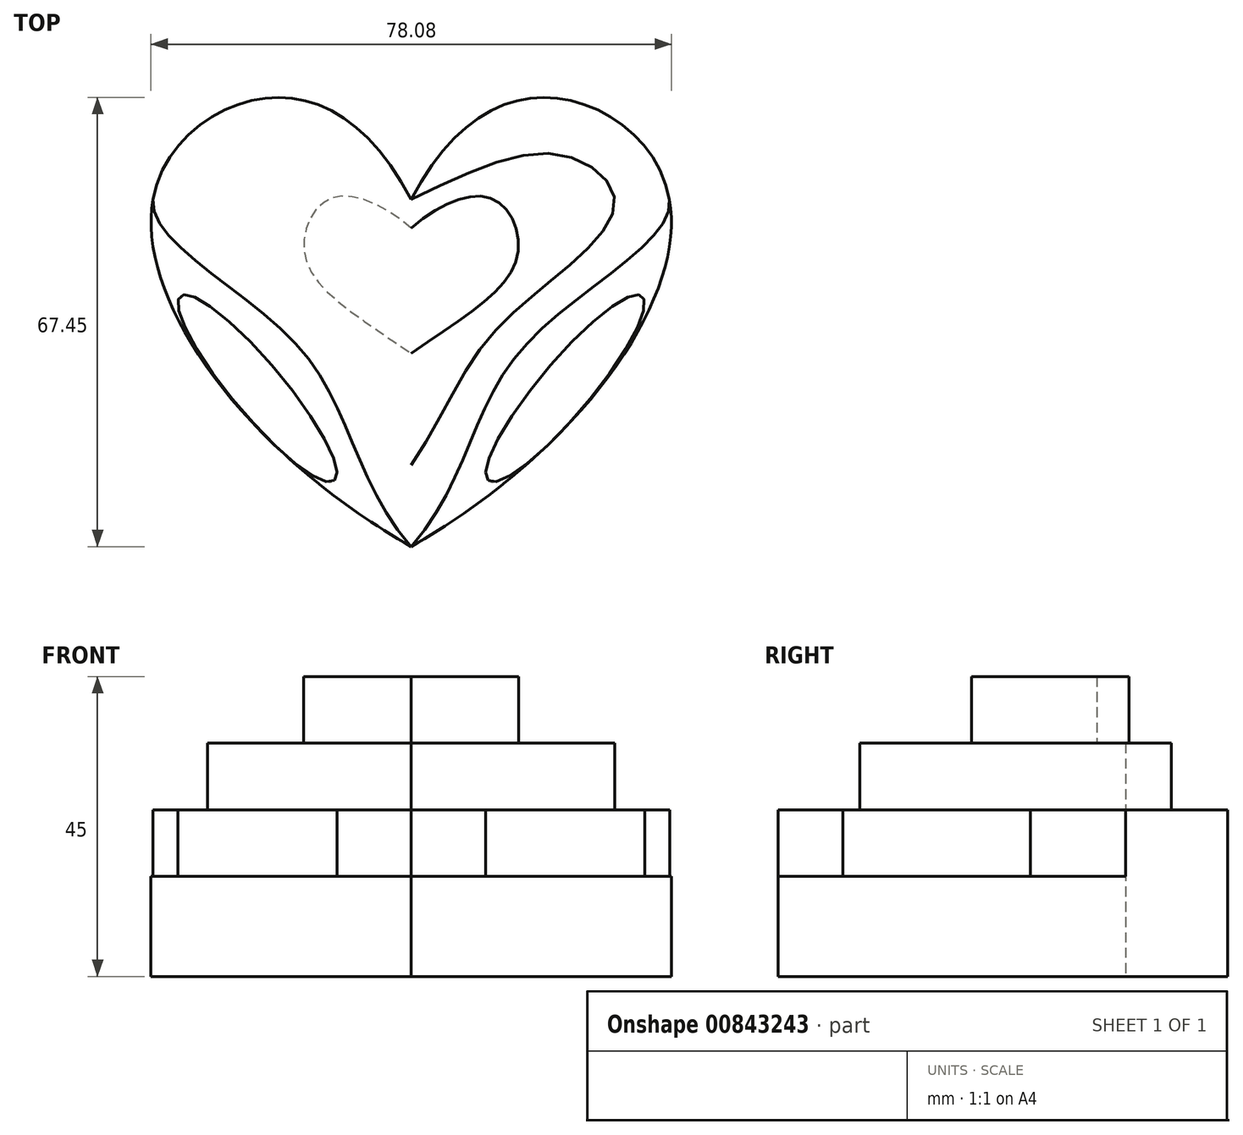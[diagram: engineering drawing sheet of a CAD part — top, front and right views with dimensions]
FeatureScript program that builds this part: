
annotation { "Feature Type Name" : "Feature", "Feature Type Description" : "" }
export const myFeature = defineFeature(function(context is Context, id is Id, definition is map)
    precondition{}
    {
        {
            var Q0;
            Q0=qCreatedBy(makeId("Top.planeOp"),FACE);
            var sketch = newSketch(context, id + "F0", { "sketchPlane" : qUnion([Q0])});
            skFitSpline(sketch, "E0", {"points": [v(0, 0) * mm, v(-21.78, 15.23) * mm, v(-38.75, 0) * mm, v(0, -52.1) * mm], "startDerivative": vector(-61.58, 117.99) * mm, "endDerivative": vector(173.73, -99.9) * mm});
            skFitSpline(sketch, "E1.MirrorCS", {"points": [v(0, 0) * mm, v(21.78, 15.23) * mm, v(38.75, 0) * mm, v(0, -52.1) * mm], "startDerivative": vector(61.58, 117.99) * mm, "endDerivative": vector(-173.73, -99.9) * mm});
            skFitSpline(sketch, "E2", {"points": [v(0, 0) * mm, v(-22.15, 6.75) * mm, v(-30.5, 0) * mm, v(-23.47, -10.1) * mm, v(-10.61, -22.06) * mm, v(0, -39.85) * mm], "startDerivative": vector(-101.95, 49.3) * mm, "endDerivative": vector(55, -77.97) * mm});
            skPoint(sketch, "E3", {"position": v(-25.47, -31.66) * mm});
            skFitSpline(sketch, "E4", {"points": [v(-38.75, 0) * mm, v(-16.95, -22.06) * mm, v(0, -52.1) * mm], "startDerivative": vector(-4.02, -40.81) * mm, "endDerivative": vector(50.77, -58.34) * mm});
            skEllipse(sketch, "E5", {"center": v(-23.08, -28.34) * mm, "majorRadius": 18.02 * mm, "minorRadius": 3.9 * mm, "majorAxis": v(0.64, -0.77)});
            skFitSpline(sketch, "E6", {"points": [v(0, -4.28) * mm, v(-12.38, 0) * mm, v(-15.9, -8.69) * mm, v(0, -23.1) * mm], "startDerivative": vector(-40.45, 34.58) * mm, "endDerivative": vector(57.5, -40.05) * mm});
            skFitSpline(sketch, "E7.MirrorCS", {"points": [v(0, 0) * mm, v(22.15, 6.75) * mm, v(30.5, 0) * mm, v(23.47, -10.1) * mm, v(10.61, -22.06) * mm, v(0, -39.85) * mm], "startDerivative": vector(101.95, 49.3) * mm, "endDerivative": vector(-55, -77.97) * mm});
            skFitSpline(sketch, "E8.MirrorCS", {"points": [v(0, -4.28) * mm, v(12.38, 0) * mm, v(15.9, -8.69) * mm, v(0, -23.1) * mm], "startDerivative": vector(40.45, 34.58) * mm, "endDerivative": vector(-57.5, -40.05) * mm});
            skFitSpline(sketch, "E9.MirrorCS", {"points": [v(38.75, 0) * mm, v(16.95, -22.06) * mm, v(0, -52.1) * mm], "startDerivative": vector(4.02, -40.81) * mm, "endDerivative": vector(-50.77, -58.34) * mm});
            skEllipse(sketch, "E10.MirrorC", {"center": v(23.08, -28.34) * mm, "majorRadius": 18.02 * mm, "minorRadius": 3.9 * mm, "majorAxis": v(-0.64, -0.77)});
            skSolve(sketch);
        }
        {
            var Q0;
            Q0=qSketchRegion(id+"F0",true);
            var Q1;
            Q1=makeQuery(id+"F0.imprint","IMPRINT",FACE,{"disambiguationData":[TD([[makeQuery(id+"F0.imprint","IMPRINT",EDGE,{"derivedFrom":sQuery(id+"F0.wireOp",EDGE,"E6")}),1.0]])]});
            extrude(context, id + "F1", {"entities" : qUnion([Q0, Q1]), "depth" : 10 * mm, "offsetDistance" : 25 * mm});
        }
        {
            var Q0;
            Q0=makeQuery(id+"F0.imprint","IMPRINT",FACE,{"disambiguationData":[TD([[makeQuery(id+"F0.imprint","IMPRINT",EDGE,{"derivedFrom":sQuery(id+"F0.wireOp",EDGE,"E5")}),1.0]])]});
            var Q1;
            Q1=makeQuery(id+"F0.imprint","IMPRINT",FACE,{"disambiguationData":[TD([[makeQuery(id+"F0.imprint","IMPRINT",EDGE,{"derivedFrom":sQuery(id+"F0.wireOp",EDGE,"E10.MirrorC")}),1.0]])]});
            extrude(context, id + "F2", {"entities" : qUnion([Q0, Q1]), "operationType" : NewBodyOperationType.ADD, "depth" : 25 * mm, "offsetDistance" : 25 * mm});
        }
        {
            var Q0;
            {var subQ1=sQuery(id+"F0.wireOp",EDGE,"E2");Q0=makeQuery(id+"F0.imprint","IMPRINT",FACE,{"disambiguationData":[TD([[makeQuery(id+"F0.imprint","IMPRINT",EDGE,{"derivedFrom":subQ1}),-1.0]])]});}
            var Q1;
            Q1=makeQuery(id+"F0.imprint","IMPRINT",FACE,{"disambiguationData":[TD([[makeQuery(id+"F0.imprint","IMPRINT",EDGE,{"derivedFrom":sQuery(id+"F0.wireOp",EDGE,"E2")}),1.0]])]});
            extrude(context, id + "F3", {"entities" : qUnion([Q0, Q1]), "operationType" : NewBodyOperationType.ADD, "depth" : 25 * mm, "offsetDistance" : 25 * mm});
        }
        {
            var Q0;
            Q0=makeQuery(id+"F0.imprint","IMPRINT",FACE,{"disambiguationData":[TD([[makeQuery(id+"F0.imprint","IMPRINT",EDGE,{"derivedFrom":sQuery(id+"F0.wireOp",EDGE,"E2")}),1.0]])]});
            extrude(context, id + "F4", {"entities" : qUnion([Q0]), "operationType" : NewBodyOperationType.ADD, "depth" : 35 * mm, "offsetDistance" : 25 * mm});
        }
        {
            var Q0;
            Q0=makeQuery(id+"F0.imprint","IMPRINT",FACE,{"disambiguationData":[TD([[makeQuery(id+"F0.imprint","IMPRINT",EDGE,{"derivedFrom":sQuery(id+"F0.wireOp",EDGE,"E6")}),1.0]])]});
            extrude(context, id + "F5", {"entities" : qUnion([Q0]), "operationType" : NewBodyOperationType.ADD, "depth" : 45 * mm, "offsetDistance" : 25 * mm});
        }
        {
            var Q0;
            {var subQ0=sQuery(id+"F0.wireOp",EDGE,"E9.MirrorCS");Q0=makeQuery(id+"F0.imprint","IMPRINT",FACE,{"disambiguationData":[TD([[makeQuery(id+"F0.imprint","IMPRINT",EDGE,{"derivedFrom":subQ0}),1.0]])]});}
            var Q1;
            Q1=makeQuery(id+"F0.imprint","IMPRINT",FACE,{"disambiguationData":[TD([[makeQuery(id+"F0.imprint","IMPRINT",EDGE,{"derivedFrom":sQuery(id+"F0.wireOp",EDGE,"E10.MirrorC")}),1.0]])]});
            var Q2;
            Q2=makeQuery(id+"F0.imprint","IMPRINT",FACE,{"disambiguationData":[TD([[makeQuery(id+"F0.imprint","IMPRINT",EDGE,{"derivedFrom":sQuery(id+"F0.wireOp",EDGE,"E5")}),1.0]])]});
            var Q3;
            {var subQ0=sQuery(id+"F0.wireOp",EDGE,"E4");Q3=makeQuery(id+"F0.imprint","IMPRINT",FACE,{"disambiguationData":[TD([[makeQuery(id+"F0.imprint","IMPRINT",EDGE,{"derivedFrom":subQ0}),-1.0]])]});}
            extrude(context, id + "F6", {"entities" : qUnion([Q0, Q1, Q2, Q3]), "operationType" : NewBodyOperationType.ADD, "depth" : 15 * mm, "offsetDistance" : 25 * mm});
        }
    });
